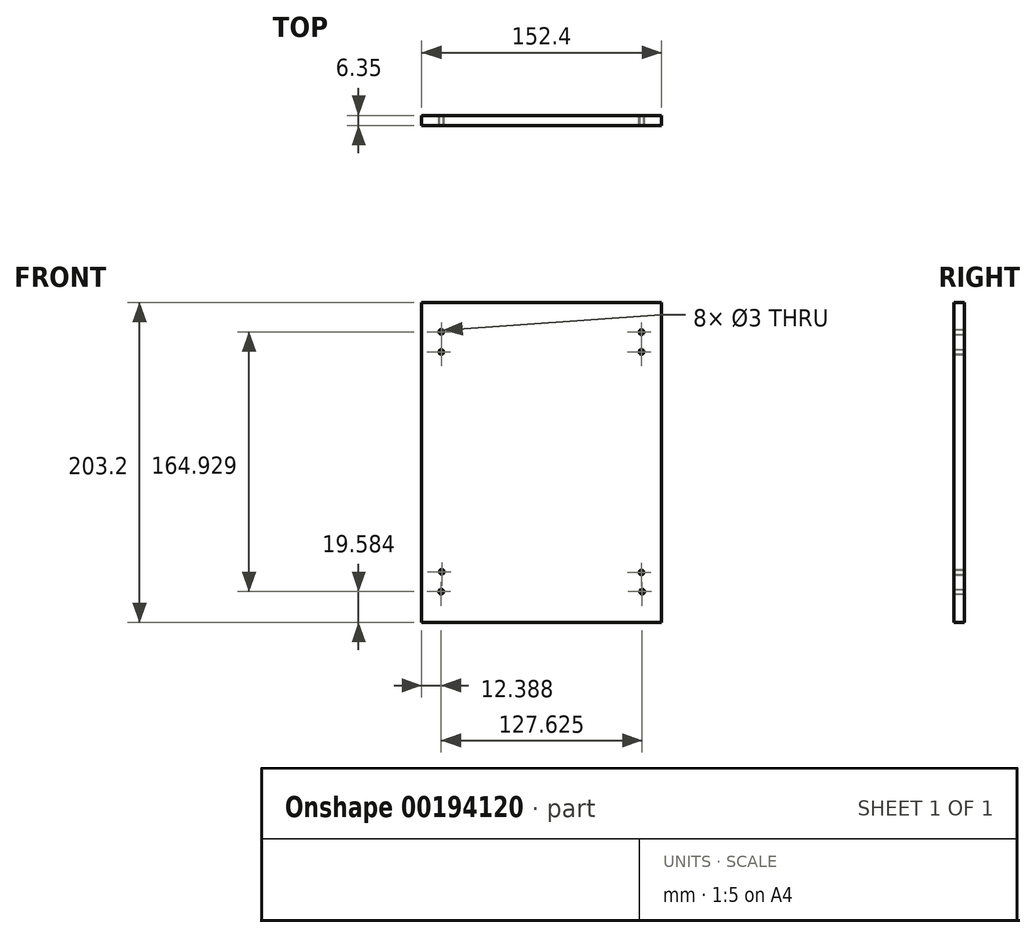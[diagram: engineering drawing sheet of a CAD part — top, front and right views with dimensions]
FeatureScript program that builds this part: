
annotation { "Feature Type Name" : "Feature", "Feature Type Description" : "" }
export const myFeature = defineFeature(function(context is Context, id is Id, definition is map)
    precondition{}
    {
        {
            var Q0;
            Q0=qCreatedBy(makeId("Front.planeOp"),FACE);
            var sketch = newSketch(context, id + "F0", { "sketchPlane" : qUnion([Q0])});
            skLineSegment(sketch, "E0.bottom", {"start": v(-76.2, 101.6) * mm, "end": v(76.2, 101.6) * mm});
            skLineSegment(sketch, "E0.top", {"start": v(-76.2, -101.6) * mm, "end": v(76.2, -101.6) * mm});
            skLineSegment(sketch, "E0.left", {"start": v(-76.2, 101.6) * mm, "end": v(-76.2, -101.6) * mm});
            skLineSegment(sketch, "E0.right", {"start": v(76.2, 101.6) * mm, "end": v(76.2, -101.6) * mm});
            skPoint(sketch, "E0.middle", {"position": v(0, 0) * mm});
            skSolve(sketch);
        }
        {
            var Q0;
            Q0=makeQuery(id+"F0.imprint","IMPRINT",FACE,{"disambiguationData":[TD([[makeQuery(id+"F0.imprint","IMPRINT",EDGE,{"derivedFrom":sQuery(id+"F0.wireOp",EDGE,"E0.bottom")}),-1.0]])]});
            extrude(context, id + "F1", {"entities" : qUnion([Q0]), "depth" : 6.35 * mm});
        }
        {
            var Q0;
            Q0=qCreatedBy(makeId("Front.planeOp"),FACE);
            var sketch = newSketch(context, id + "F2", { "sketchPlane" : qUnion([Q0])});
            skCircle(sketch, "E1", {"center": v(-63.73, 82.91) * mm, "radius": 1.5 * mm});
            skCircle(sketch, "E2", {"center": v(-63.73, 70.18) * mm, "radius": 1.5 * mm});
            skSolve(sketch);
        }
        {
            var Q0;
            Q0=qCreatedBy(makeId("Front.planeOp"),FACE);
            var sketch = newSketch(context, id + "F3", { "sketchPlane" : qUnion([Q0])});
            skCircle(sketch, "E3", {"center": v(63.42, 82.8) * mm, "radius": 1.5 * mm});
            skSolve(sketch);
        }
        {
            var Q0;
            Q0=qCreatedBy(makeId("Front.planeOp"),FACE);
            var sketch = newSketch(context, id + "F4", { "sketchPlane" : qUnion([Q0])});
            skCircle(sketch, "E4", {"center": v(63.42, 70.27) * mm, "radius": 1.5 * mm});
            skSolve(sketch);
        }
        {
            var Q0;
            Q0=qCreatedBy(makeId("Front.planeOp"),FACE);
            var sketch = newSketch(context, id + "F5", { "sketchPlane" : qUnion([Q0])});
            skCircle(sketch, "E5", {"center": v(-63.81, -82.02) * mm, "radius": 1.5 * mm});
            skSolve(sketch);
        }
        {
            var Q0;
            Q0=qCreatedBy(makeId("Front.planeOp"),FACE);
            var sketch = newSketch(context, id + "F6", { "sketchPlane" : qUnion([Q0])});
            skCircle(sketch, "E6", {"center": v(-63.42, -69.49) * mm, "radius": 1.5 * mm});
            skSolve(sketch);
        }
        {
            var Q0;
            Q0=qCreatedBy(makeId("Front.planeOp"),FACE);
            var sketch = newSketch(context, id + "F7", { "sketchPlane" : qUnion([Q0])});
            skCircle(sketch, "E7", {"center": v(63.81, -82.02) * mm, "radius": 1.5 * mm});
            skSolve(sketch);
        }
        {
            var Q0;
            Q0=qCreatedBy(makeId("Front.planeOp"),FACE);
            var sketch = newSketch(context, id + "F8", { "sketchPlane" : qUnion([Q0])});
            skCircle(sketch, "E8", {"center": v(63.42, -69.88) * mm, "radius": 1.5 * mm});
            skSolve(sketch);
        }
        {
            var Q0;
            Q0=makeQuery(id+"F2.imprint","IMPRINT",FACE,{"disambiguationData":[TD([[makeQuery(id+"F2.imprint","IMPRINT",EDGE,{"derivedFrom":sQuery(id+"F2.wireOp",EDGE,"E1")}),1.0]])]});
            var Q1;
            Q1=makeQuery(id+"F2.imprint","IMPRINT",FACE,{"disambiguationData":[TD([[makeQuery(id+"F2.imprint","IMPRINT",EDGE,{"derivedFrom":sQuery(id+"F2.wireOp",EDGE,"E2")}),1.0]])]});
            extrude(context, id + "F9", {"entities" : qUnion([Q0, Q1]), "operationType" : NewBodyOperationType.REMOVE, "depth" : 50.8 * mm});
        }
        {
            var Q0;
            Q0=makeQuery(id+"F3.imprint","IMPRINT",FACE,{"disambiguationData":[TD([[makeQuery(id+"F3.imprint","IMPRINT",EDGE,{"derivedFrom":sQuery(id+"F3.wireOp",EDGE,"E3")}),1.0]])]});
            var Q1;
            Q1=makeQuery(id+"F4.imprint","IMPRINT",FACE,{"disambiguationData":[TD([[makeQuery(id+"F4.imprint","IMPRINT",EDGE,{"derivedFrom":sQuery(id+"F4.wireOp",EDGE,"E4")}),1.0]])]});
            extrude(context, id + "F10", {"entities" : qUnion([Q0, Q1]), "operationType" : NewBodyOperationType.REMOVE, "depth" : 127 * mm});
        }
        {
            var Q0;
            Q0=makeQuery(id+"F6.imprint","IMPRINT",FACE,{"disambiguationData":[TD([[makeQuery(id+"F6.imprint","IMPRINT",EDGE,{"derivedFrom":sQuery(id+"F6.wireOp",EDGE,"E6")}),1.0]])]});
            var Q1;
            Q1=makeQuery(id+"F5.imprint","IMPRINT",FACE,{"disambiguationData":[TD([[makeQuery(id+"F5.imprint","IMPRINT",EDGE,{"derivedFrom":sQuery(id+"F5.wireOp",EDGE,"E5")}),1.0]])]});
            extrude(context, id + "F11", {"entities" : qUnion([Q0, Q1]), "operationType" : NewBodyOperationType.REMOVE, "depth" : 127 * mm});
        }
        {
            var Q0;
            Q0=makeQuery(id+"F8.imprint","IMPRINT",FACE,{"disambiguationData":[TD([[makeQuery(id+"F8.imprint","IMPRINT",EDGE,{"derivedFrom":sQuery(id+"F8.wireOp",EDGE,"E8")}),1.0]])]});
            var Q1;
            Q1=makeQuery(id+"F7.imprint","IMPRINT",FACE,{"disambiguationData":[TD([[makeQuery(id+"F7.imprint","IMPRINT",EDGE,{"derivedFrom":sQuery(id+"F7.wireOp",EDGE,"E7")}),1.0]])]});
            extrude(context, id + "F12", {"entities" : qUnion([Q0, Q1]), "operationType" : NewBodyOperationType.REMOVE, "depth" : 76.2 * mm});
        }
    });
